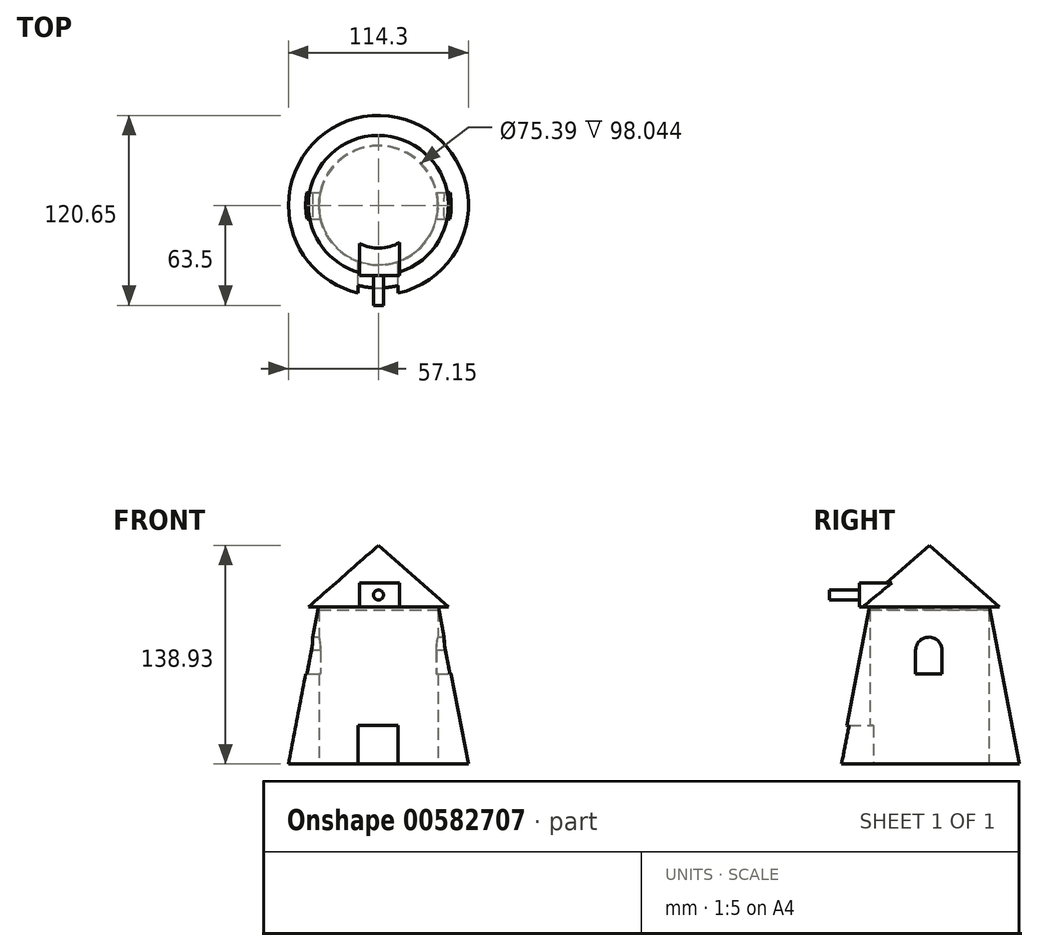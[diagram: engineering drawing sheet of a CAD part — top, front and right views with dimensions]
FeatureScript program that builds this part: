
annotation { "Feature Type Name" : "Feature", "Feature Type Description" : "" }
export const myFeature = defineFeature(function(context is Context, id is Id, definition is map)
    precondition{}
    {
        {
            var Q0;
            Q0=qCreatedBy(makeId("Front.planeOp"),FACE);
            var sketch = newSketch(context, id + "F0", { "sketchPlane" : qUnion([Q0])});
            skLineSegment(sketch, "E0", {"start": v(-38.1, 38.75) * mm, "end": v(-57.15, -61.05) * mm});
            skLineSegment(sketch, "E1", {"start": v(-57.15, -61.05) * mm, "end": v(0, -61.05) * mm});
            skLineSegment(sketch, "E2", {"start": v(0, -61.05) * mm, "end": v(0, 38.75) * mm});
            skLineSegment(sketch, "E3", {"start": v(-38.1, 38.75) * mm, "end": v(0, 38.75) * mm});
            skLineSegment(sketch, "E4", {"start": v(-38.1, 38.75) * mm, "end": v(-44.45, 38.75) * mm});
            skLineSegment(sketch, "E5", {"start": v(-44.45, 38.75) * mm, "end": v(0, 77.88) * mm});
            skLineSegment(sketch, "E6", {"start": v(0, 77.88) * mm, "end": v(0, 38.75) * mm});
            skSolve(sketch);
        }
        {
            var Q0;
            Q0 = qSketchRegion(id + "F0", true);
            var Q1;
            Q1=sQuery(id+"F0.wireOp",EDGE,"E2");
            revolve(context, id + "F1", {"entities" : qUnion([Q0]), "axis" : qUnion([Q1]), "revolveType" : RevolveType.FULL});
        }
        {
            var Q0;
            Q0=qCreatedBy(makeId("Front.planeOp"),FACE);
            var sketch = newSketch(context, id + "F2", { "sketchPlane" : qUnion([Q0])});
            skLineSegment(sketch, "E7", {"start": v(0, -36.57) * mm, "end": v(-12.93, -36.57) * mm});
            skLineSegment(sketch, "E8", {"start": v(-12.93, -36.57) * mm, "end": v(-12.93, -61.05) * mm});
            skLineSegment(sketch, "E9", {"start": v(-12.93, -61.05) * mm, "end": v(0, -61.05) * mm});
            skLineSegment(sketch, "E10", {"start": v(0, -61.05) * mm, "end": v(12.47, -61.05) * mm});
            skLineSegment(sketch, "E11", {"start": v(12.47, -61.05) * mm, "end": v(12.47, -36.57) * mm});
            skLineSegment(sketch, "E12", {"start": v(12.47, -36.57) * mm, "end": v(0, -36.57) * mm});
            skSolve(sketch);
        }
        {
            var Q0;
            Q0 = qSketchRegion(id + "F2", true);
            extrude(context, id + "F3", {"entities" : qUnion([Q0]), "operationType" : NewBodyOperationType.REMOVE, "depth" : 87.88 * mm, "offsetDistance" : 25.4 * mm});
        }
        {
            var Q0;
            Q0=makeQuery(id+"F1.opRevolve","SWEPT_FACE",FACE,{"disambiguationData":[OSD([sQuery(id+"F0.wireOp",EDGE,"E1")])]});
            var sketch = newSketch(context, id + "F4", { "sketchPlane" : qUnion([Q0])});
            skCircle(sketch, "E13", {"center": v(0, 0) * mm, "radius": 37.7 * mm});
            skSolve(sketch);
        }
        {
            var Q0;
            Q0 = qSketchRegion(id + "F4", true);
            extrude(context, id + "F5", {"entities" : qUnion([Q0]), "operationType" : NewBodyOperationType.REMOVE, "oppositeDirection" : true, "depth" : 98.04 * mm, "offsetDistance" : 25.4 * mm});
        }
        {
            var Q0;
            Q0=qCreatedBy(makeId("Front.planeOp"),FACE);
            var sketch = newSketch(context, id + "F6", { "sketchPlane" : qUnion([Q0])});
            skLineSegment(sketch, "E14", {"start": v(0, 38.75) * mm, "end": v(13.39, 38.75) * mm});
            skLineSegment(sketch, "E15", {"start": v(13.39, 38.75) * mm, "end": v(13.39, 53.99) * mm});
            skLineSegment(sketch, "E16", {"start": v(13.39, 53.99) * mm, "end": v(0, 53.99) * mm});
            skLineSegment(sketch, "E17", {"start": v(0, 53.99) * mm, "end": v(-12.01, 53.99) * mm});
            skLineSegment(sketch, "E18", {"start": v(-12.01, 53.99) * mm, "end": v(-12.01, 38.75) * mm});
            skLineSegment(sketch, "E19", {"start": v(-12.01, 38.75) * mm, "end": v(0, 38.75) * mm});
            skSolve(sketch);
        }
        {
            var Q0;
            Q0 = qSketchRegion(id + "F6", true);
            extrude(context, id + "F7", {"entities" : qUnion([Q0]), "operationType" : NewBodyOperationType.ADD, "depth" : 44.45 * mm, "offsetDistance" : 25.4 * mm});
        }
        {
            var Q0;
            Q0=makeQuery(id+"F7.opExtrude","CAP_FACE",FACE,{"disambiguationData":[OSD([sQuery(id+"F6.wireOp",EDGE,"E14"),sQuery(id+"F6.wireOp",EDGE,"E15"),sQuery(id+"F6.wireOp",EDGE,"E16"),sQuery(id+"F6.wireOp",EDGE,"E17"),sQuery(id+"F6.wireOp",EDGE,"E18"),sQuery(id+"F6.wireOp",EDGE,"E19")])],"isStart":false});
            var sketch = newSketch(context, id + "F8", { "sketchPlane" : qUnion([Q0])});
            skCircle(sketch, "E20", {"center": v(0, 46.37) * mm, "radius": 3.18 * mm});
            skPoint(sketch, "E20.centerSnap0", {"position": v(-12.01, 46.37) * mm});
            skSolve(sketch);
        }
        {
            var Q0;
            Q0=makeQuery(id+"F8.imprint","IMPRINT",FACE,{"disambiguationData":[TD([[makeQuery(id+"F8.imprint","IMPRINT",EDGE,{"derivedFrom":sQuery(id+"F8.wireOp",EDGE,"E20")}),1.0]])]});
            extrude(context, id + "F9", {"entities" : qUnion([Q0]), "operationType" : NewBodyOperationType.ADD, "depth" : 19.05 * mm, "offsetDistance" : 25.4 * mm});
        }
        {
            var Q0;
            Q0=qCreatedBy(makeId("Right.planeOp"),FACE);
            var sketch = newSketch(context, id + "F10", { "sketchPlane" : qUnion([Q0])});
            skLineSegment(sketch, "E21", {"start": v(-8.73, 11.17) * mm, "end": v(-8.73, -3.67) * mm});
            skLineSegment(sketch, "E22", {"start": v(-8.73, -3.67) * mm, "end": v(8.15, -3.67) * mm});
            skLineSegment(sketch, "E23", {"start": v(8.15, -3.67) * mm, "end": v(8.15, 11.46) * mm});
            skArc(sketch, "E24", {"start": v(8.15, 11.46) * mm, "mid": v(-0.43, 19.61) * mm, "end": v(-8.73, 11.17) * mm});
            skSolve(sketch);
        }
        {
            var Q0;
            Q0 = qSketchRegion(id + "F10", true);
            extrude(context, id + "F11", {"entities" : qUnion([Q0]), "operationType" : NewBodyOperationType.REMOVE, "oppositeDirection" : true, "depth" : 67.56 * mm, "offsetDistance" : 25.4 * mm, "hasSecondDirection" : true, "secondDirectionOppositeDirection" : false, "secondDirectionDepth" : 63 * mm});
        }
    });
